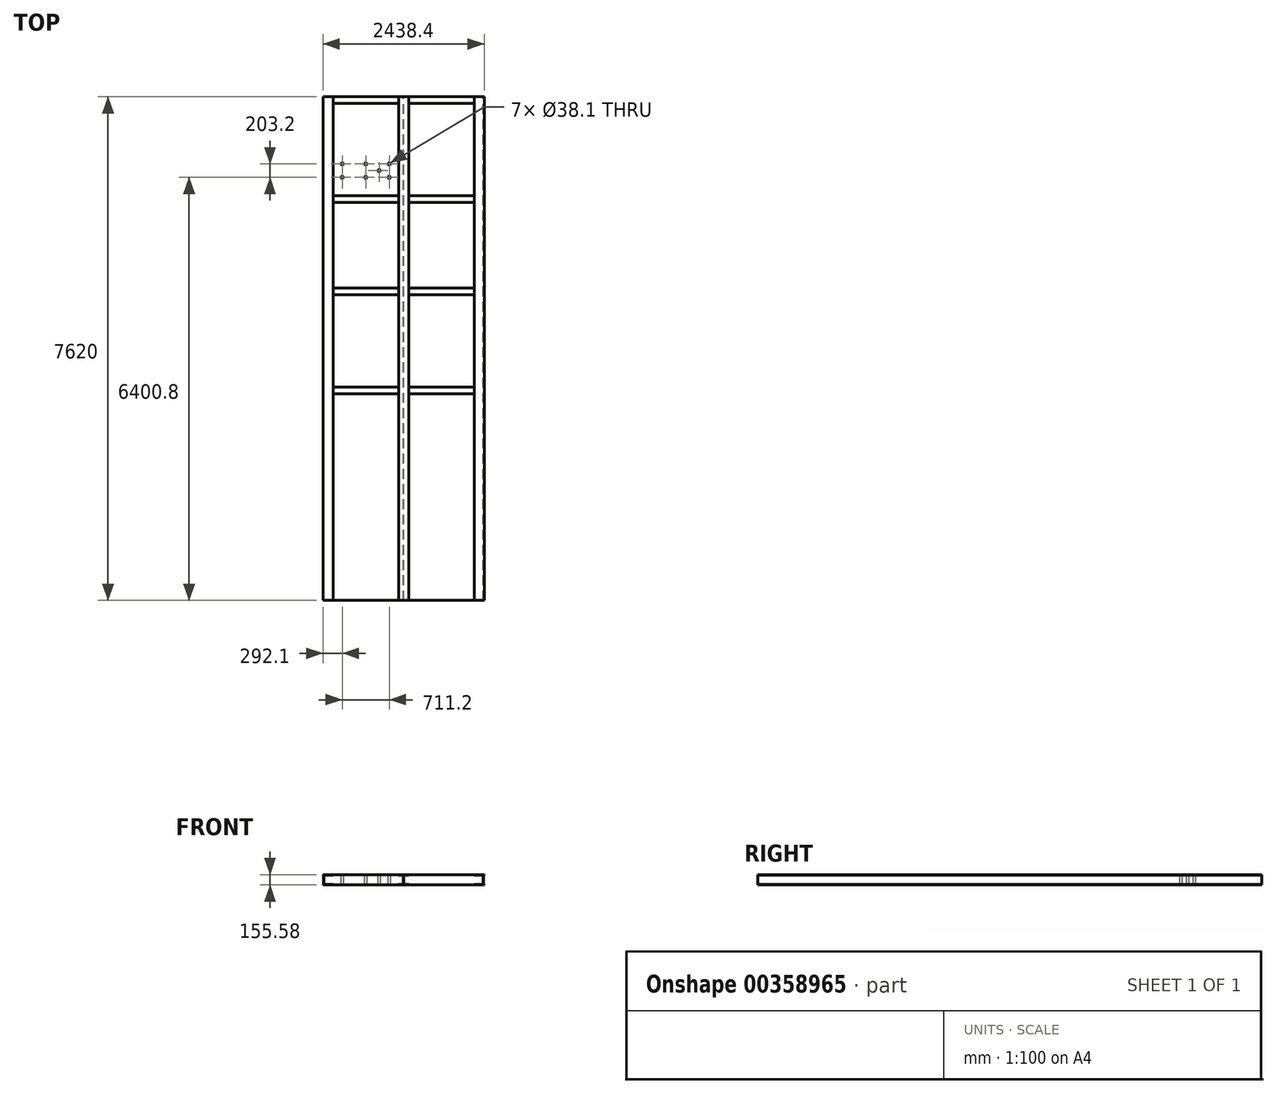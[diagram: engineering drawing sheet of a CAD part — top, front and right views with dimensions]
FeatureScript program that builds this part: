
annotation { "Feature Type Name" : "Feature", "Feature Type Description" : "" }
export const myFeature = defineFeature(function(context is Context, id is Id, definition is map)
    precondition{}
    {
        {
            var Q0;
            Q0=qCreatedBy(makeId("Front.planeOp"),FACE);
            var sketch = newSketch(context, id + "F0", { "sketchPlane" : qUnion([Q0])});
            skLineSegment(sketch, "E0.bottom", {"start": v(0, 0) * mm, "end": v(152.4, 0) * mm});
            skLineSegment(sketch, "E0.top", {"start": v(0, -6.35) * mm, "end": v(152.4, -6.35) * mm});
            skLineSegment(sketch, "E0.left", {"start": v(0, 0) * mm, "end": v(0, -6.35) * mm});
            skLineSegment(sketch, "E0.right", {"start": v(152.4, 0) * mm, "end": v(152.4, -6.35) * mm});
            skLineSegment(sketch, "E1.bottom", {"start": v(0, -149.23) * mm, "end": v(152.4, -149.23) * mm});
            skLineSegment(sketch, "E1.top", {"start": v(0, -155.58) * mm, "end": v(152.4, -155.57) * mm});
            skLineSegment(sketch, "E1.left", {"start": v(0, -149.23) * mm, "end": v(0, -155.58) * mm});
            skLineSegment(sketch, "E1.right", {"start": v(152.4, -149.22) * mm, "end": v(152.4, -155.57) * mm});
            skLineSegment(sketch, "E2.bottom", {"start": v(144.46, -6.35) * mm, "end": v(138.11, -6.35) * mm});
            skLineSegment(sketch, "E2.top", {"start": v(144.46, -149.23) * mm, "end": v(138.11, -149.23) * mm});
            skLineSegment(sketch, "E2.left", {"start": v(144.46, -6.35) * mm, "end": v(144.46, -149.23) * mm});
            skLineSegment(sketch, "E2.right", {"start": v(138.11, -6.35) * mm, "end": v(138.11, -149.23) * mm});
            skSolve(sketch);
        }
        {
            var Q0;
            Q0=qSketchRegion(id+"F0",true);
            extrude(context, id + "F1", {"entities" : qUnion([Q0]), "depth" : 7620 * mm});
        }
        {
            var Q0;
            Q0=qCreatedBy(makeId("Front.planeOp"),FACE);
            var sketch = newSketch(context, id + "F2", { "sketchPlane" : qUnion([Q0])});
            skLineSegment(sketch, "E3.bottom", {"start": v(-2286, 0) * mm, "end": v(-2133.6, 0) * mm});
            skLineSegment(sketch, "E3.top", {"start": v(-2286, -6.35) * mm, "end": v(-2133.6, -6.35) * mm});
            skLineSegment(sketch, "E3.left", {"start": v(-2286, 0) * mm, "end": v(-2286, -6.35) * mm});
            skLineSegment(sketch, "E3.right", {"start": v(-2133.6, 0) * mm, "end": v(-2133.6, -6.35) * mm});
            skLineSegment(sketch, "E4.bottom", {"start": v(-2286, -149.23) * mm, "end": v(-2133.6, -149.23) * mm});
            skLineSegment(sketch, "E4.top", {"start": v(-2286, -155.58) * mm, "end": v(-2133.6, -155.58) * mm});
            skLineSegment(sketch, "E4.left", {"start": v(-2286, -149.23) * mm, "end": v(-2286, -155.58) * mm});
            skLineSegment(sketch, "E4.right", {"start": v(-2133.6, -149.23) * mm, "end": v(-2133.6, -155.58) * mm});
            skLineSegment(sketch, "E5.bottom", {"start": v(-2278.06, -6.35) * mm, "end": v(-2271.71, -6.35) * mm});
            skLineSegment(sketch, "E5.top", {"start": v(-2278.06, -149.23) * mm, "end": v(-2271.71, -149.23) * mm});
            skLineSegment(sketch, "E5.left", {"start": v(-2278.06, -6.35) * mm, "end": v(-2278.06, -149.23) * mm});
            skLineSegment(sketch, "E5.right", {"start": v(-2271.71, -6.35) * mm, "end": v(-2271.71, -149.23) * mm});
            skSolve(sketch);
        }
        {
            var Q0;
            Q0=qSketchRegion(id+"F2",true);
            extrude(context, id + "F3", {"entities" : qUnion([Q0]), "depth" : 7620 * mm});
        }
        {
            var Q0;
            Q0=qCreatedBy(makeId("Front.planeOp"),FACE);
            var sketch = newSketch(context, id + "F4", { "sketchPlane" : qUnion([Q0])});
            skLineSegment(sketch, "E6.0", {"start": v(-2286, 0) * mm, "end": v(-2133.6, 0) * mm});
            skPoint(sketch, "E7.0", {"position": v(-2286, -3.18) * mm});
            skLineSegment(sketch, "E8.0", {"start": v(-2286, 0) * mm, "end": v(-2286, -6.35) * mm});
            skLineSegment(sketch, "E9.0.0", {"start": v(-2286, -6.35) * mm, "end": v(-2278.06, -6.35) * mm, "construction": true});
            skLineSegment(sketch, "E9.0.1", {"start": v(-2278.06, -6.35) * mm, "end": v(-2278.06, -149.23) * mm, "construction": true});
            skLineSegment(sketch, "E9.0.2", {"start": v(-2278.06, -149.23) * mm, "end": v(-2286, -149.23) * mm, "construction": true});
            skLineSegment(sketch, "E9.0.3", {"start": v(-2286, -149.23) * mm, "end": v(-2286, -155.58) * mm, "construction": true});
            skLineSegment(sketch, "E9.0.4", {"start": v(-2286, -155.58) * mm, "end": v(-2133.6, -155.58) * mm, "construction": true});
            skLineSegment(sketch, "E9.0.5", {"start": v(-2133.6, -155.58) * mm, "end": v(-2133.6, -149.23) * mm, "construction": true});
            skLineSegment(sketch, "E9.0.6", {"start": v(-2133.6, -149.23) * mm, "end": v(-2271.71, -149.23) * mm, "construction": true});
            skLineSegment(sketch, "E9.0.7", {"start": v(-2271.71, -149.23) * mm, "end": v(-2271.71, -6.35) * mm, "construction": true});
            skLineSegment(sketch, "E9.0.8", {"start": v(-2271.71, -6.35) * mm, "end": v(-2133.6, -6.35) * mm, "construction": true});
            skLineSegment(sketch, "E9.0.9", {"start": v(-2133.6, -6.35) * mm, "end": v(-2133.6, 0) * mm, "construction": true});
            skLineSegment(sketch, "E9.0.10", {"start": v(-2133.6, 0) * mm, "end": v(-2286, 0) * mm, "construction": true});
            skLineSegment(sketch, "E9.0.11", {"start": v(-2286, 0) * mm, "end": v(-2286, -6.35) * mm, "construction": true});
            skLineSegment(sketch, "E10.0", {"start": v(0, 0) * mm, "end": v(152.4, 0) * mm, "construction": true});
            skLineSegment(sketch, "E11.0", {"start": v(0, -6.35) * mm, "end": v(138.11, -6.35) * mm, "construction": true});
            skLineSegment(sketch, "E12.0", {"start": v(144.46, -6.35) * mm, "end": v(144.46, -149.23) * mm, "construction": true});
            skLineSegment(sketch, "E13.0", {"start": v(138.11, -6.35) * mm, "end": v(138.11, -149.23) * mm, "construction": true});
            skLineSegment(sketch, "E14.0", {"start": v(0, -149.23) * mm, "end": v(138.11, -149.23) * mm, "construction": true});
            skPoint(sketch, "E15.0", {"position": v(0, -152.4) * mm});
            skLineSegment(sketch, "E16", {"start": v(152.4, 0) * mm, "end": v(-2286, 0) * mm, "construction": true});
            skLineSegment(sketch, "E17", {"start": v(-1066.8, 457.17) * mm, "end": v(-1066.8, -578.58) * mm, "construction": true});
            skLineSegment(sketch, "E18.bottom", {"start": v(-1143, 0) * mm, "end": v(-990.6, 0) * mm});
            skLineSegment(sketch, "E18.top", {"start": v(-1143, -6.35) * mm, "end": v(-990.6, -6.35) * mm});
            skLineSegment(sketch, "E18.left", {"start": v(-1143, 0) * mm, "end": v(-1143, -6.35) * mm});
            skLineSegment(sketch, "E18.right", {"start": v(-990.6, 0) * mm, "end": v(-990.6, -6.35) * mm});
            skLineSegment(sketch, "E19.bottom", {"start": v(-1143, -149.23) * mm, "end": v(-990.6, -149.23) * mm});
            skLineSegment(sketch, "E19.top", {"start": v(-1143, -155.58) * mm, "end": v(-990.6, -155.58) * mm});
            skLineSegment(sketch, "E19.left", {"start": v(-1143, -149.23) * mm, "end": v(-1143, -155.58) * mm});
            skLineSegment(sketch, "E19.right", {"start": v(-990.6, -149.23) * mm, "end": v(-990.6, -155.58) * mm});
            skLineSegment(sketch, "E20.bottom", {"start": v(-1069.97, -6.35) * mm, "end": v(-1063.62, -6.35) * mm});
            skLineSegment(sketch, "E20.top", {"start": v(-1069.97, -149.23) * mm, "end": v(-1063.62, -149.23) * mm});
            skLineSegment(sketch, "E20.left", {"start": v(-1069.97, -6.35) * mm, "end": v(-1069.97, -149.23) * mm});
            skLineSegment(sketch, "E20.right", {"start": v(-1063.62, -6.35) * mm, "end": v(-1063.62, -149.23) * mm});
            skSolve(sketch);
        }
        {
            var Q0;
            Q0=qSketchRegion(id+"F4",true);
            extrude(context, id + "F5", {"entities" : qUnion([Q0]), "depth" : 7620 * mm});
        }
        {
            var Q0;
            Q0=qCreatedBy(makeId("Front.planeOp"),FACE);
            var sketch = newSketch(context, id + "F6", { "sketchPlane" : qUnion([Q0])});
            skLineSegment(sketch, "E21.0", {"start": v(-2286, 0) * mm, "end": v(-2133.6, 0) * mm, "construction": true});
            skLineSegment(sketch, "E22.0", {"start": v(-2133.6, 0) * mm, "end": v(-2133.6, -6.35) * mm, "construction": true});
            skLineSegment(sketch, "E23.0", {"start": v(-2271.71, -6.35) * mm, "end": v(-2133.6, -6.35) * mm, "construction": true});
            skLineSegment(sketch, "E24.0", {"start": v(-2271.71, -6.35) * mm, "end": v(-2271.71, -149.23) * mm, "construction": true});
            skLineSegment(sketch, "E25.0", {"start": v(-2278.06, -6.35) * mm, "end": v(-2278.06, -149.23) * mm, "construction": true});
            skLineSegment(sketch, "E26.0", {"start": v(-2286, -6.35) * mm, "end": v(-2278.06, -6.35) * mm, "construction": true});
            skPoint(sketch, "E27.0", {"position": v(-2286, -3.18) * mm});
            skLineSegment(sketch, "E28.0", {"start": v(-2286, 0) * mm, "end": v(-2286, -6.35) * mm, "construction": true});
            skLineSegment(sketch, "E29.0", {"start": v(-2271.71, -149.23) * mm, "end": v(-2133.6, -149.23) * mm, "construction": true});
            skLineSegment(sketch, "E30.0", {"start": v(-2133.6, -149.23) * mm, "end": v(-2133.6, -155.58) * mm, "construction": true});
            skLineSegment(sketch, "E31.0", {"start": v(-2286, -155.58) * mm, "end": v(-2133.6, -155.58) * mm, "construction": true});
            skPoint(sketch, "E32.0", {"position": v(-2286, -152.4) * mm});
            skLineSegment(sketch, "E33.0", {"start": v(-2286, -149.23) * mm, "end": v(-2278.06, -149.23) * mm, "construction": true});
            skLineSegment(sketch, "E34.0", {"start": v(-2286, -149.23) * mm, "end": v(-2286, -155.58) * mm, "construction": true});
            skLineSegment(sketch, "E35.0", {"start": v(-1143, 0) * mm, "end": v(-990.6, 0) * mm, "construction": true});
            skPoint(sketch, "E36.0", {"position": v(-1143, -3.18) * mm});
            skLineSegment(sketch, "E37.0", {"start": v(-1143, -6.35) * mm, "end": v(-1069.97, -6.35) * mm, "construction": true});
            skLineSegment(sketch, "E38.0", {"start": v(-1143, 0) * mm, "end": v(-1143, -6.35) * mm, "construction": true});
            skLineSegment(sketch, "E39.0", {"start": v(-1069.97, -6.35) * mm, "end": v(-1069.97, -149.23) * mm, "construction": true});
            skLineSegment(sketch, "E40.0", {"start": v(-1143, -149.23) * mm, "end": v(-1069.97, -149.23) * mm, "construction": true});
            skLineSegment(sketch, "E41.0", {"start": v(-1143, -149.23) * mm, "end": v(-1143, -155.58) * mm, "construction": true});
            skLineSegment(sketch, "E42.0", {"start": v(-990.6, -149.23) * mm, "end": v(-990.6, -155.58) * mm, "construction": true});
            skLineSegment(sketch, "E43.0", {"start": v(-1063.62, -149.23) * mm, "end": v(-990.6, -149.23) * mm, "construction": true});
            skLineSegment(sketch, "E44.0", {"start": v(-1063.62, -6.35) * mm, "end": v(-1063.62, -149.23) * mm, "construction": true});
            skLineSegment(sketch, "E45.0", {"start": v(-1063.62, -6.35) * mm, "end": v(-990.6, -6.35) * mm, "construction": true});
            skLineSegment(sketch, "E46.0", {"start": v(-990.6, 0) * mm, "end": v(-990.6, -6.35) * mm, "construction": true});
            skLineSegment(sketch, "E47.0", {"start": v(0, 0) * mm, "end": v(152.4, 0) * mm, "construction": true});
            skLineSegment(sketch, "E48.0", {"start": v(0, 0) * mm, "end": v(0, -6.35) * mm, "construction": true});
            skLineSegment(sketch, "E49.0", {"start": v(0, -6.35) * mm, "end": v(138.11, -6.35) * mm, "construction": true});
            skLineSegment(sketch, "E50.0", {"start": v(138.11, -6.35) * mm, "end": v(138.11, -149.23) * mm, "construction": true});
            skLineSegment(sketch, "E51.0", {"start": v(0, -149.23) * mm, "end": v(138.11, -149.23) * mm, "construction": true});
            skLineSegment(sketch, "E52.0", {"start": v(0, -149.23) * mm, "end": v(0, -155.58) * mm, "construction": true});
            skLineSegment(sketch, "E53.0", {"start": v(0, -155.58) * mm, "end": v(152.4, -155.57) * mm, "construction": true});
            skLineSegment(sketch, "E54", {"start": v(0, 0) * mm, "end": v(0, -6.35) * mm});
            skLineSegment(sketch, "E55", {"start": v(0, -6.35) * mm, "end": v(138.11, -6.35) * mm});
            skLineSegment(sketch, "E56", {"start": v(138.11, -6.35) * mm, "end": v(138.11, -149.23) * mm});
            skLineSegment(sketch, "E57", {"start": v(138.11, -149.23) * mm, "end": v(0, -149.23) * mm});
            skLineSegment(sketch, "E58", {"start": v(0, -149.23) * mm, "end": v(0, -155.58) * mm});
            skLineSegment(sketch, "E59", {"start": v(0, -155.58) * mm, "end": v(-990.6, -155.58) * mm});
            skLineSegment(sketch, "E60", {"start": v(-990.6, -149.23) * mm, "end": v(-1063.62, -149.23) * mm});
            skLineSegment(sketch, "E61", {"start": v(-990.6, -155.58) * mm, "end": v(-990.6, -149.23) * mm});
            skLineSegment(sketch, "E62", {"start": v(-1063.62, -149.23) * mm, "end": v(-1063.62, -6.35) * mm});
            skLineSegment(sketch, "E63", {"start": v(-1063.62, -6.35) * mm, "end": v(-990.6, -6.35) * mm});
            skLineSegment(sketch, "E64", {"start": v(-990.6, -6.35) * mm, "end": v(-990.6, 0) * mm});
            skLineSegment(sketch, "E65", {"start": v(-990.6, 0) * mm, "end": v(0, 0) * mm});
            skLineSegment(sketch, "E66", {"start": v(-1143, 0) * mm, "end": v(-1143, -6.35) * mm});
            skLineSegment(sketch, "E67", {"start": v(-1143, -6.35) * mm, "end": v(-1069.97, -6.35) * mm});
            skLineSegment(sketch, "E68", {"start": v(-1069.97, -6.35) * mm, "end": v(-1069.97, -149.23) * mm});
            skLineSegment(sketch, "E69", {"start": v(-1069.97, -149.23) * mm, "end": v(-1143, -149.23) * mm});
            skLineSegment(sketch, "E70", {"start": v(-1143, -149.23) * mm, "end": v(-1143, -155.58) * mm});
            skLineSegment(sketch, "E71", {"start": v(-1143, -155.58) * mm, "end": v(-2133.6, -155.58) * mm});
            skLineSegment(sketch, "E72", {"start": v(-2133.6, -155.58) * mm, "end": v(-2133.6, -149.23) * mm});
            skLineSegment(sketch, "E73", {"start": v(-2133.6, -149.23) * mm, "end": v(-2271.71, -149.23) * mm});
            skLineSegment(sketch, "E74", {"start": v(-2271.71, -149.23) * mm, "end": v(-2271.71, -6.35) * mm});
            skLineSegment(sketch, "E75", {"start": v(-2271.71, -6.35) * mm, "end": v(-2133.6, -6.35) * mm});
            skLineSegment(sketch, "E76", {"start": v(-2133.6, -6.35) * mm, "end": v(-2133.6, 0) * mm});
            skLineSegment(sketch, "E77", {"start": v(-2133.6, 0) * mm, "end": v(-1143, 0) * mm});
            skSolve(sketch);
        }
        {
            var Q0;
            Q0=qSketchRegion(id+"F6",true);
            extrude(context, id + "F7", {"entities" : qUnion([Q0]), "depth" : 7620 * mm});
        }
        {
            var Q0;
            Q0=makeQuery(id+"F7.opExtrude","SWEPT_FACE",FACE,{"disambiguationData":[OSD([sQuery(id+"F6.wireOp",EDGE,"E65")])]});
            var sketch = newSketch(context, id + "F8", { "sketchPlane" : qUnion([Q0])});
            skLineSegment(sketch, "E78", {"start": v(-990.6, -1498.6) * mm, "end": v(0, -1498.6) * mm, "construction": true});
            skLineSegment(sketch, "E79.bottom", {"start": v(-990.6, -1498.6) * mm, "end": v(0, -1498.6) * mm});
            skLineSegment(sketch, "E79.top", {"start": v(-990.6, -1600.2) * mm, "end": v(0, -1600.2) * mm});
            skLineSegment(sketch, "E79.left", {"start": v(-990.6, -1498.6) * mm, "end": v(-990.6, -1600.2) * mm});
            skLineSegment(sketch, "E79.right", {"start": v(0, -1498.6) * mm, "end": v(0, -1600.2) * mm});
            skLineSegment(sketch, "E80.0", {"start": v(-1143, -7620) * mm, "end": v(-1143, 0) * mm, "construction": true});
            skLineSegment(sketch, "E81.0", {"start": v(-2133.6, -7620) * mm, "end": v(-2133.6, 0) * mm, "construction": true});
            skLineSegment(sketch, "E82.0", {"start": v(-990.6, -7620) * mm, "end": v(-990.6, 0) * mm, "construction": true});
            skLineSegment(sketch, "E83.0", {"start": v(0, -7620) * mm, "end": v(0, 0) * mm, "construction": true});
            skLineSegment(sketch, "E84", {"start": v(-1143, -1498.6) * mm, "end": v(-2133.6, -1498.6) * mm, "construction": true});
            skLineSegment(sketch, "E85.bottom", {"start": v(-2133.6, -1498.6) * mm, "end": v(-1143, -1498.6) * mm});
            skLineSegment(sketch, "E85.top", {"start": v(-2133.6, -1600.2) * mm, "end": v(-1143, -1600.2) * mm});
            skLineSegment(sketch, "E85.left", {"start": v(-2133.6, -1498.6) * mm, "end": v(-2133.6, -1600.2) * mm});
            skLineSegment(sketch, "E85.right", {"start": v(-1143, -1498.6) * mm, "end": v(-1143, -1600.2) * mm});
            skLineSegment(sketch, "E86.bottom", {"start": v(-2133.6, 0) * mm, "end": v(-1143, 0) * mm});
            skLineSegment(sketch, "E86.top", {"start": v(-2133.6, -101.6) * mm, "end": v(-1143, -101.6) * mm});
            skLineSegment(sketch, "E86.left", {"start": v(-2133.6, 0) * mm, "end": v(-2133.6, -101.6) * mm});
            skLineSegment(sketch, "E86.right", {"start": v(-1143, 0) * mm, "end": v(-1143, -101.6) * mm});
            skLineSegment(sketch, "E87.bottom", {"start": v(-990.6, 0) * mm, "end": v(0, 0) * mm});
            skLineSegment(sketch, "E87.top", {"start": v(-990.6, -101.6) * mm, "end": v(0, -101.6) * mm});
            skLineSegment(sketch, "E87.left", {"start": v(-990.6, 0) * mm, "end": v(-990.6, -101.6) * mm});
            skLineSegment(sketch, "E87.right", {"start": v(0, 0) * mm, "end": v(0, -101.6) * mm});
            skLineSegment(sketch, "E88", {"start": v(-2133.6, -2997.2) * mm, "end": v(0, -2997.2) * mm, "construction": true});
            skLineSegment(sketch, "E89", {"start": v(-2133.6, -4495.8) * mm, "end": v(0, -4495.8) * mm, "construction": true});
            skLineSegment(sketch, "E90.bottom", {"start": v(0, -2997.2) * mm, "end": v(-990.6, -2997.2) * mm});
            skLineSegment(sketch, "E90.top", {"start": v(0, -2895.6) * mm, "end": v(-990.6, -2895.6) * mm});
            skLineSegment(sketch, "E90.left", {"start": v(0, -2997.2) * mm, "end": v(0, -2895.6) * mm});
            skLineSegment(sketch, "E90.right", {"start": v(-990.6, -2997.2) * mm, "end": v(-990.6, -2895.6) * mm});
            skLineSegment(sketch, "E91.bottom", {"start": v(-1143, -2997.2) * mm, "end": v(-2133.6, -2997.2) * mm});
            skLineSegment(sketch, "E91.top", {"start": v(-1143, -2895.6) * mm, "end": v(-2133.6, -2895.6) * mm});
            skLineSegment(sketch, "E91.left", {"start": v(-1143, -2997.2) * mm, "end": v(-1143, -2895.6) * mm});
            skLineSegment(sketch, "E91.right", {"start": v(-2133.6, -2997.2) * mm, "end": v(-2133.6, -2895.6) * mm});
            skLineSegment(sketch, "E92.bottom", {"start": v(0, -4495.8) * mm, "end": v(-990.6, -4495.8) * mm});
            skLineSegment(sketch, "E92.top", {"start": v(0, -4394.2) * mm, "end": v(-990.6, -4394.2) * mm});
            skLineSegment(sketch, "E92.left", {"start": v(0, -4495.8) * mm, "end": v(0, -4394.2) * mm});
            skLineSegment(sketch, "E92.right", {"start": v(-990.6, -4495.8) * mm, "end": v(-990.6, -4394.2) * mm});
            skLineSegment(sketch, "E93.bottom", {"start": v(-2133.6, -4495.8) * mm, "end": v(-1143, -4495.8) * mm});
            skLineSegment(sketch, "E93.top", {"start": v(-2133.6, -4394.2) * mm, "end": v(-1143, -4394.2) * mm});
            skLineSegment(sketch, "E93.left", {"start": v(-2133.6, -4495.8) * mm, "end": v(-2133.6, -4394.2) * mm});
            skLineSegment(sketch, "E93.right", {"start": v(-1143, -4495.8) * mm, "end": v(-1143, -4394.2) * mm});
            skSolve(sketch);
        }
        {
            var Q0;
            Q0=qSketchRegion(id+"F8",true);
            extrude(context, id + "F9", {"entities" : qUnion([Q0]), "oppositeDirection" : true, "depth" : 6.35 * mm});
        }
        {
            var Q0;
            Q0=makeQuery(id+"F3.opExtrude","SWEPT_FACE",FACE,{"disambiguationData":[OSD([sQuery(id+"F2.wireOp",EDGE,"E3.bottom")])]});
            var sketch = newSketch(context, id + "F10", { "sketchPlane" : qUnion([Q0])});
            skLineSegment(sketch, "E94.0", {"start": v(-2286, -7620) * mm, "end": v(-2286, 0) * mm, "construction": true});
            skLineSegment(sketch, "E95.0", {"start": v(-2286, 0) * mm, "end": v(-2133.6, 0) * mm, "construction": true});
            skLineSegment(sketch, "E96.0", {"start": v(-990.6, -7620) * mm, "end": v(-990.6, 0) * mm, "construction": true});
            skLineSegment(sketch, "E97", {"start": v(-2286, -914.4) * mm, "end": v(-990.6, -914.4) * mm, "construction": true});
            skLineSegment(sketch, "E98", {"start": v(-2286, -1320.8) * mm, "end": v(-990.6, -1320.8) * mm, "construction": true});
            skLineSegment(sketch, "E99", {"start": v(-2286, -1117.6) * mm, "end": v(-990.6, -1117.6) * mm, "construction": true});
            skLineSegment(sketch, "E100", {"start": v(-2286, -1016) * mm, "end": v(-990.6, -1016) * mm, "construction": true});
            skLineSegment(sketch, "E101", {"start": v(-2286, -1219.2) * mm, "end": v(-990.6, -1219.2) * mm, "construction": true});
            skLineSegment(sketch, "E102", {"start": v(-1993.9, -914.4) * mm, "end": v(-1993.9, -1320.8) * mm, "construction": true});
            skLineSegment(sketch, "E103", {"start": v(-1638.3, -914.4) * mm, "end": v(-1638.3, -1320.8) * mm, "construction": true});
            skLineSegment(sketch, "E104", {"start": v(-1282.7, -914.4) * mm, "end": v(-1282.7, -1320.8) * mm, "construction": true});
            skLineSegment(sketch, "E105", {"start": v(-1841.5, -914.4) * mm, "end": v(-1841.5, -1320.8) * mm, "construction": true});
            skCircle(sketch, "E106", {"center": v(-1993.9, -1016) * mm, "radius": 19.05 * mm});
            skCircle(sketch, "E107", {"center": v(-1993.9, -1219.2) * mm, "radius": 19.05 * mm});
            skCircle(sketch, "E108", {"center": v(-1638.3, -1016) * mm, "radius": 19.05 * mm});
            skCircle(sketch, "E109", {"center": v(-1638.3, -1219.2) * mm, "radius": 19.05 * mm});
            skCircle(sketch, "E110", {"center": v(-1282.7, -1016) * mm, "radius": 19.05 * mm});
            skCircle(sketch, "E111", {"center": v(-1282.7, -1219.2) * mm, "radius": 19.05 * mm});
            skLineSegment(sketch, "E112", {"start": v(-1435.1, -914.4) * mm, "end": v(-1435.1, -1320.8) * mm, "construction": true});
            skCircle(sketch, "E113", {"center": v(-1435.1, -1117.6) * mm, "radius": 19.05 * mm});
            skSolve(sketch);
        }
        {
            var Q0;
            Q0 = qSketchRegion(id + "F10", true);
            extrude(context, id + "F11", {"entities" : qUnion([Q0]), "operationType" : NewBodyOperationType.REMOVE, "endBound" : BoundingType.THROUGH_ALL, "oppositeDirection" : true, "depth" : 25.4 * mm});
        }
    });
